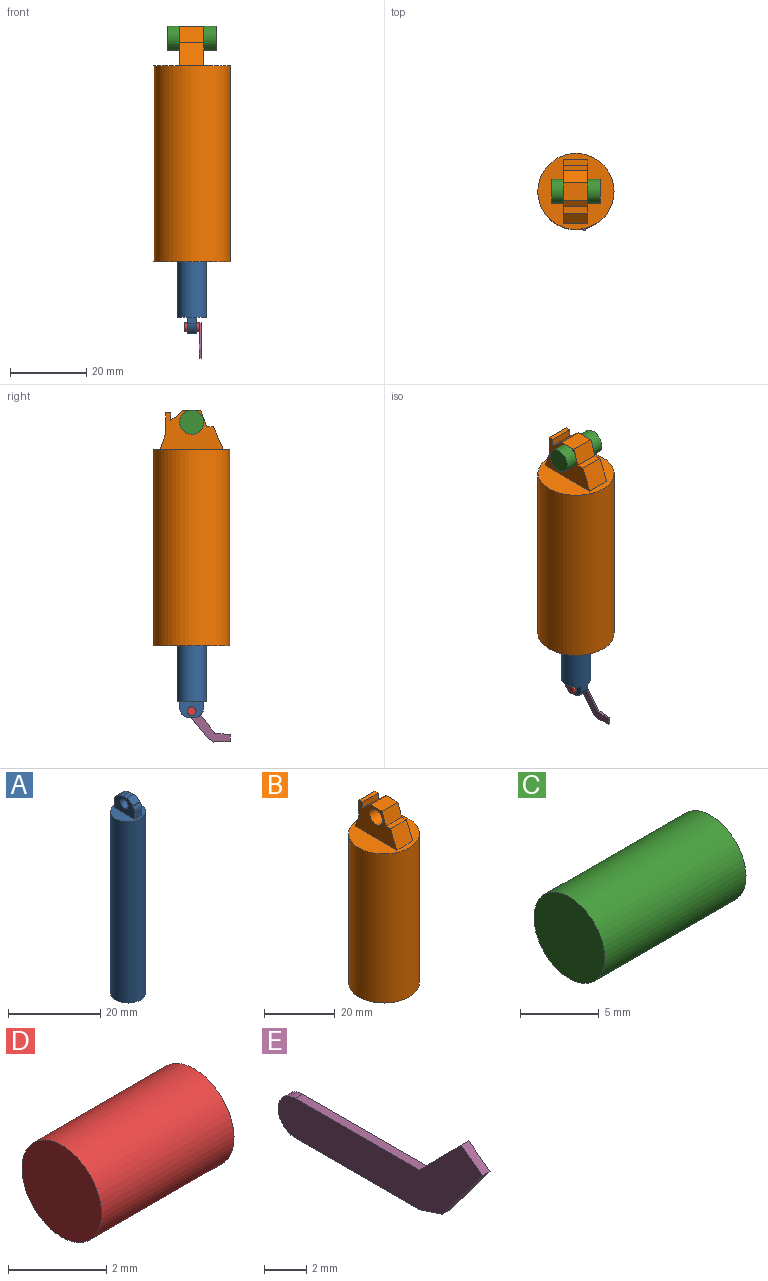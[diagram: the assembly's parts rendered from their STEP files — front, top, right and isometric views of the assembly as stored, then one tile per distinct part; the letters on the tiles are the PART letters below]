
ASSEMBLY  parts=5 mates=4
PART A: 15 faces, bbox 7.6x7.6x52.6 mm
  f0: plane 7.62x7.62mm, normal (0,0,1), area 31.8mm2, adj f1,f3,f4,f5,f6
  f1: cylinder r=3.81mm len=48.26mm, axis (0,0,-1), area 1155.3mm2, adj f0,f2
  f2: plane 7.62x7.62mm, normal (0,0,-1), area 45.6mm2, adj f1
  f3: plane 6.31x4.31mm, normal (1,0,0), area 20.1mm2, adj f0,f4,f6,f7,f8,f9,f10,f11
  f4: plane 2.19x1.69mm, normal (0,1,0), area 3.7mm2, adj f0,f3,f5,f14
  f5: plane 6.31x4.31mm, normal (-1,0,0), area 20.1mm2, adj f0,f4,f6,f7,f8,f9,f10,f11
  f6: plane 2.19x1.69mm, normal (0,-1,0), area 3.7mm2, adj f0,f3,f5,f11
  f7: plane 2.19x0.08mm, normal (0,-0.79,0.61), area 0.2mm2, adj f3,f5,f11,f12
  f8: plane 2.19x1.11mm, normal (0,0,1), area 2.4mm2, adj f3,f5,f12,f13
  f9: plane 2.19x0.08mm, normal (0,0.79,0.61), area 0.2mm2, adj f3,f5,f13,f14
  f10: cylinder r=1.14mm len=2.29mm, axis (1,0,0), area 15.7mm2, adj f3,f5
  f11: cylinder r=2.54mm len=2.19mm, axis (-1,0,0), area 3.7mm2, adj f3,f5,f6,f7
  f12: cylinder r=2.54mm len=2.19mm, axis (1,0,0), area 5.1mm2, adj f3,f5,f7,f8
  f13: cylinder r=2.54mm len=2.19mm, axis (-1,0,0), area 5.1mm2, adj f3,f5,f8,f9
  f14: cylinder r=2.54mm len=2.19mm, axis (-1,0,0), area 3.7mm2, adj f3,f4,f5,f9
PART B: 17 faces, bbox 20x20x61.8 mm
  f0: plane 16.6x10.41mm, normal (1,0,0), area 104.4mm2, adj f2,f7,f8,f9,f10,f11,f12,f13
  f1: plane 16.6x10.41mm, normal (-1,0,0), area 104.4mm2, adj f2,f7,f8,f9,f10,f11,f12,f13
  f2: plane 19.96x19.96mm, normal (0,0,1), area 208.1mm2, adj f0,f1,f3,f7,f15
  f3: cylinder r=9.98mm len=51.42mm, axis (0,0,1), area 3224.6mm2, adj f2,f4
  f4: plane 19.96x19.96mm, normal (0,0,-1), area 267.3mm2, adj f3,f5
  f5: cylinder r=3.81mm len=48.26mm, axis (0,0,-1), area 1155.3mm2, adj f4,f6
  f6: plane 7.62x7.62mm, normal (0,0,-1), area 45.6mm2, adj f5
  f7: plane 6.31x6.02mm, normal (0,-0.92,0.4), area 41.4mm2, adj f0,f1,f2,f8
  f8: plane 6.31x1.83mm, normal (0,0,1), area 11.5mm2, adj f0,f1,f7,f9
  f9: plane 6.31x4.4mm, normal (0,-0.95,0.32), area 29.3mm2, adj f0,f1,f8,f10
  f10: plane 6.31x4.6mm, normal (0,0,1), area 29mm2, adj f0,f1,f9,f11
  f11: plane 6.31x3.24mm, normal (0,0.65,0.76), area 26.9mm2, adj f0,f1,f10,f12
  f12: plane 6.31x2.03mm, normal (0,-1,0), area 12.8mm2, adj f0,f1,f11,f13
  f13: plane 6.31x1.39mm, normal (0,0,1), area 8.8mm2, adj f0,f1,f12,f14
  f14: plane 6.31x5.5mm, normal (0,1,0), area 34.7mm2, adj f0,f1,f13,f15
  f15: plane 6.31x4.17mm, normal (0,0.94,0.33), area 27.9mm2, adj f0,f1,f2,f14
  f16: cylinder r=2.54mm len=6.31mm, axis (1,0,0), area 100.8mm2, adj f0,f1
PART C: 3 faces, bbox 12.7x6.4x6.4 mm
  f0: cylinder r=3.17mm len=12.7mm, axis (-1,0,0), area 253.4mm2, adj f1,f2
  f1: plane 6.35x6.35mm, normal (1,0,0), area 31.7mm2, adj f0
  f2: plane 6.35x6.35mm, normal (-1,0,0), area 31.7mm2, adj f0
PART D: 3 faces, bbox 3.8x2.3x2.3 mm
  f0: cylinder r=1.14mm len=3.81mm, axis (-1,0,0), area 27.4mm2, adj f1,f2
  f1: plane 2.29x2.29mm, normal (1,0,0), area 4.1mm2, adj f0
  f2: plane 2.29x2.29mm, normal (-1,0,0), area 4.1mm2, adj f0
PART E: 9 faces, bbox 0.5x13.7x5.1 mm
  f0: plane 1.56x0.51mm, normal (0,-0.31,-0.95), area 0.8mm2, adj f1,f6,f7,f8
  f1: plane 8.3x0.51mm, normal (0,0,-1), area 4.2mm2, adj f0,f2,f7,f8
  f2: cylinder r=1.14mm len=2.29mm, axis (-1,0,0), area 1.8mm2, adj f1,f3,f7,f8
  f3: plane 8.3x0.51mm, normal (0,0,1), area 4.2mm2, adj f2,f4,f7,f8
  f4: plane 2.85x2.81mm, normal (0,0.71,0.7), area 2mm2, adj f3,f5,f7,f8
  f5: plane 1.42x1.06mm, normal (0,-0.6,0.8), area 0.9mm2, adj f4,f6,f7,f8
  f6: plane 3.56x2.67mm, normal (0,-0.8,-0.6), area 2.3mm2, adj f0,f5,f7,f8
  f7: plane 13.67x5.14mm, normal (1,0,0), area 31.5mm2, adj f0,f1,f2,f3,f4,f5,f6
  f8: plane 13.67x5.14mm, normal (-1,0,0), area 31.5mm2, adj f0,f1,f2,f3,f4,f5,f6
PLACE A rot(axis=(1,0,0),180deg) t=(-24.71,7.39,16.3)mm
PLACE B t=(-24.71,7.39,-10.82)mm fixed
PLACE C rot(axis=(-1,0,0),25.9deg) t=(-24.71,7.39,65.39)mm
PLACE D rot(axis=(1,0,0),51.2deg) t=(-24.71,7.39,-10.39)mm
PLACE E rot(axis=(1,0,0),51.2deg) t=(-22.55,7.39,-10.39)mm
MATE revolute C.f0 <-> B.f16  axis (-1,0,0) through (-24.71,7.39,65.39)mm
MATE revolute D.f0 <-> A.f10  axis (-1,0,0) through (-24.71,7.39,-10.39)mm
MATE fastened E.f2 <-> D.f0  axis (-1,0,0) through (-22.81,7.39,-10.39)mm
MATE slider B.f5 <-> A.f1  axis (0,0,-1) through (-24.71,7.39,30.9)mm
